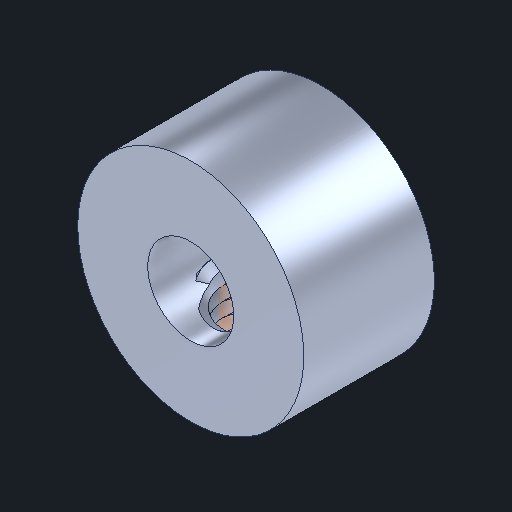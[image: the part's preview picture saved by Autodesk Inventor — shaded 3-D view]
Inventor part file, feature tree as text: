
AUTODESK INVENTOR PART (.ipt)
format: ipt  version: 2024 (Build 280153000, 153)  size: 590,336 bytes
history: native  units: in
note: dims shown in document units (in); Inventor stores cm internally (conversion verified against a paired STEP export)
features: other x6, sketch x3, plane x1
ambient origin geometry x8: Origin, YZ Plane, XZ Plane, XY Plane, X Axis, Y Axis, Z Axis, Center Point
bodies: Body1 (feature_tree), Body2 (feature_tree)
feature tree (10):
  other  "Shaft Collar Metal.ipt"
  other  "NONE::Shaft Collar Metal.ipt"
  other  "TaggingFeature1"
  sketch  "Sketch1"  dims[d0=0.3937in]
  sketch  "Sketch2"
  sketch  "Sketch3"
  plane  "Work Plane1"
  other  "Srf1"
  parser-record x1  (decoder bookkeeping rows leaked as tree rows — omitted from the tree; the rows remain in map.json)
  other  "Srf1::Derived"
